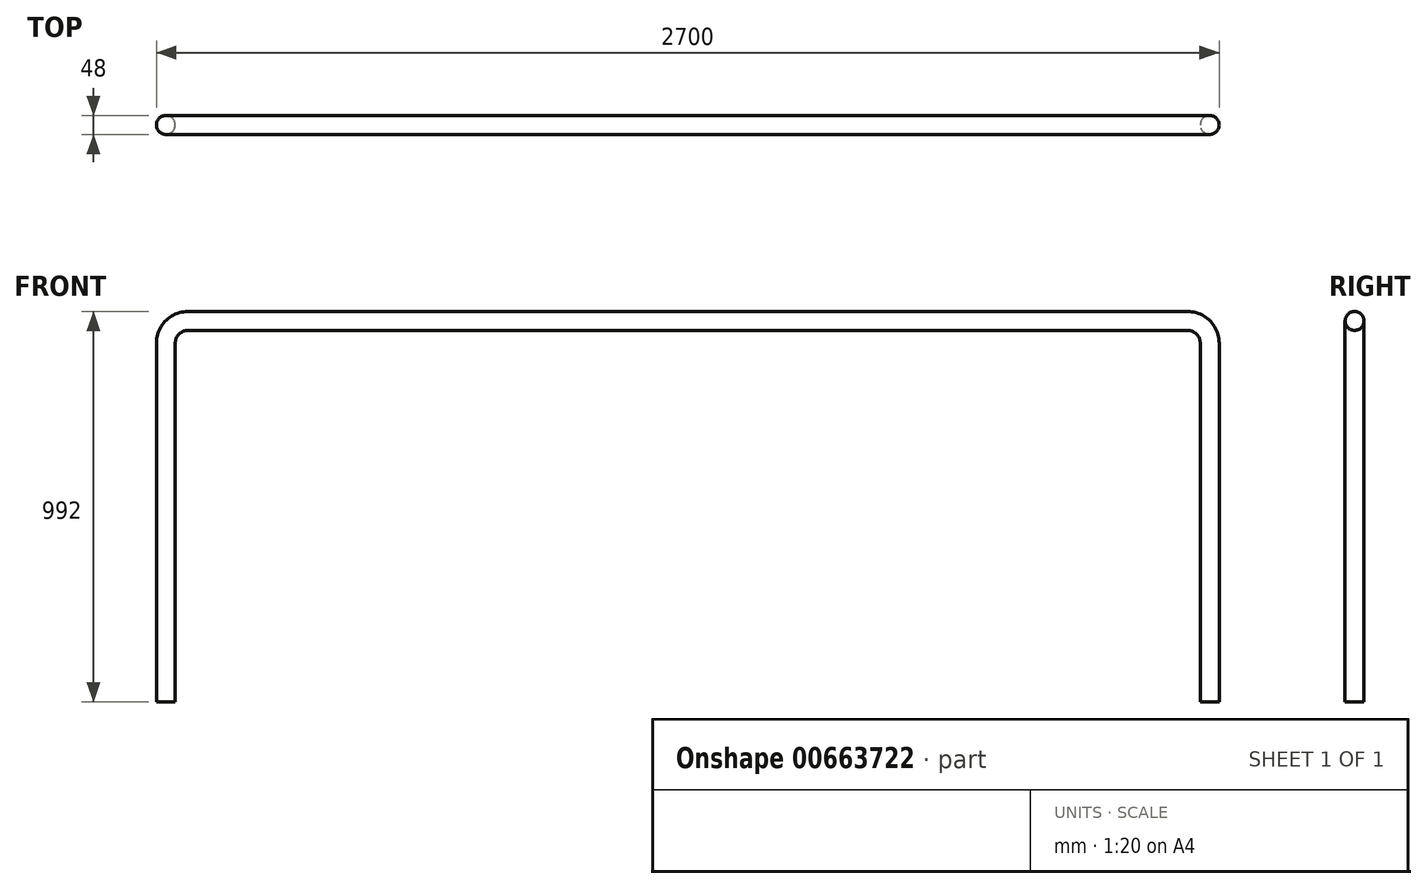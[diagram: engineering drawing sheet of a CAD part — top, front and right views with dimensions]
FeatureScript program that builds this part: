
annotation { "Feature Type Name" : "Feature", "Feature Type Description" : "" }
export const myFeature = defineFeature(function(context is Context, id is Id, definition is map)
    precondition{}
    {
        {
            var Q0;
            Q0=qCreatedBy(makeId("Front.planeOp"),FACE);
            var sketch = newSketch(context, id + "F0", { "sketchPlane" : qUnion([Q0])});
            skLineSegment(sketch, "E0", {"start": v(80, 0) * mm, "end": v(2620, 0) * mm});
            skLineSegment(sketch, "E1", {"start": v(0, -80) * mm, "end": v(0, -992) * mm});
            skPoint(sketch, "E2.visualSharp", {"position": v(0, 0) * mm});
            skArc(sketch, "E2.filletArc", {"start": v(80, 0) * mm, "mid": v(23.43, -23.43) * mm, "end": v(0, -80) * mm});
            skLineSegment(sketch, "E3", {"start": v(2700, -80) * mm, "end": v(2700, -992) * mm});
            skPoint(sketch, "E4.visualSharp", {"position": v(2700, 0) * mm});
            skArc(sketch, "E4.filletArc", {"start": v(2700, -80) * mm, "mid": v(2676.57, -23.43) * mm, "end": v(2620, 0) * mm});
            skLineSegment(sketch, "E5", {"start": v(80, 0) * mm, "end": v(80, -80) * mm});
            skSolve(sketch);
        }
        {
            var Q0;
            Q0=sQuery(id+"F0.wireOp",VERTEX,"E1.end");
            var Q1;
            Q1=sQuery(id+"F0.wireOp",EDGE,"E1");
            cPlane(context, id + "F1", {"entities" : qUnion([Q0, Q1]), "cplaneType" : CPlaneType.CURVE_POINT, "offset" : 25 * mm, "width" : 150 * mm, "height" : 150 * mm});
        }
        {
            var Q0;
            Q0=qCreatedBy(id+"F1.planeOp",FACE);
            var sketch = newSketch(context, id + "F2", { "sketchPlane" : qUnion([Q0])});
            skLineSegment(sketch, "E6", {"start": v(0, 0) * mm, "end": v(24, 0) * mm});
            skCircle(sketch, "E7", {"center": v(24, 0) * mm, "radius": 24 * mm});
            skSolve(sketch);
        }
        {
            var Q0;
            Q0=makeQuery(id+"F2.imprint","IMPRINT",FACE,{"disambiguationData":[TD([[makeQuery(id+"F2.imprint","IMPRINT",EDGE,{"derivedFrom":sQuery(id+"F2.wireOp",EDGE,"E7")}),1.0]])]});
            var Q1;
            Q1=sQuery(id+"F0.wireOp",EDGE,"E1");
            var Q2;
            Q2=sQuery(id+"F0.wireOp",EDGE,"E0");
            var Q3;
            Q3=sQuery(id+"F0.wireOp",EDGE,"E2.filletArc");
            var Q4;
            Q4=sQuery(id+"F0.wireOp",EDGE,"E4.filletArc");
            var Q5;
            Q5=sQuery(id+"F0.wireOp",EDGE,"E3");
            sweep(context, id + "F3", {"profiles" : qUnion([Q0]), "path" : qUnion([Q1, Q2, Q3, Q4, Q5])});
        }
    });
